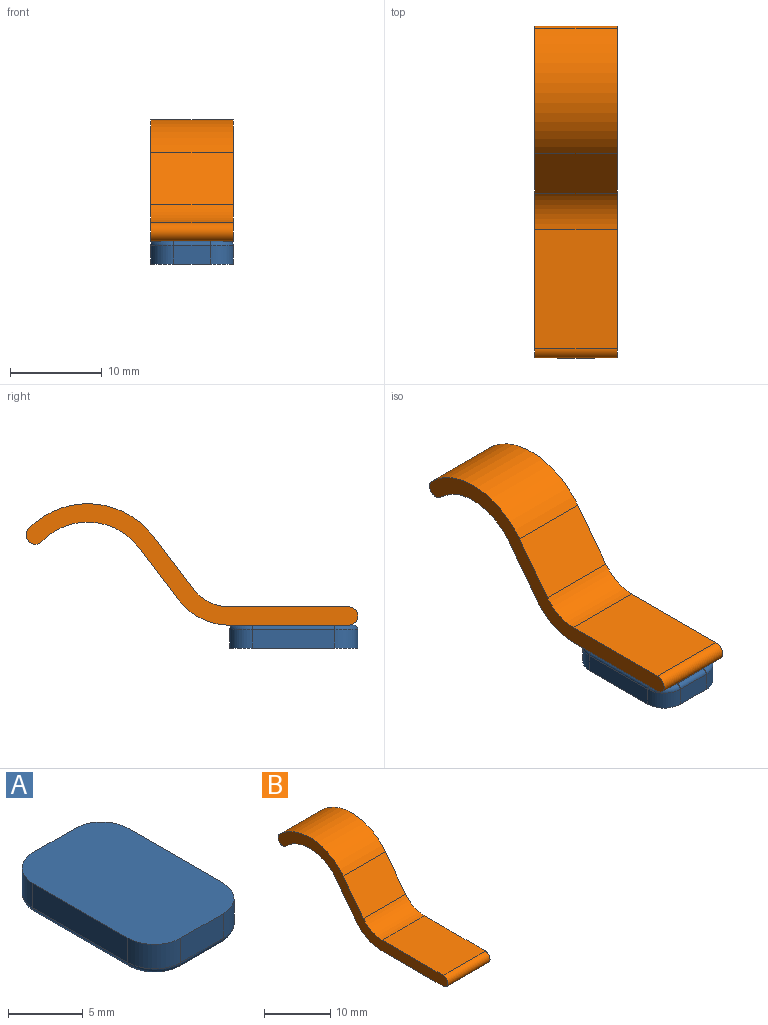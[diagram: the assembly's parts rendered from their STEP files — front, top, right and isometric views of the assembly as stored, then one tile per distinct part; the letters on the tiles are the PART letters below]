
ASSEMBLY  parts=2 mates=1
PART A: 27 faces, bbox 9.4x14.4x2.5 mm
  f0: plane 9x2mm, normal (1,0,0), area 18mm2, adj f1,f7,f8,f17
  f1: cylinder r=2.5mm len=2.5mm, axis (0,0,-1), area 7.9mm2, adj f0,f2,f8,f15
  f2: plane 4x2mm, normal (0,1,0), area 8mm2, adj f1,f3,f8,f16
  f3: cylinder r=2.5mm len=2.5mm, axis (0,0,-1), area 7.9mm2, adj f2,f4,f8,f18
  f4: plane 9x2mm, normal (-1,0,0), area 18mm2, adj f3,f5,f8,f20
  f5: cylinder r=2.5mm len=2.5mm, axis (0,0,-1), area 7.9mm2, adj f4,f6,f8,f22
  f6: plane 4x2mm, normal (0,-1,0), area 8mm2, adj f5,f7,f8,f21
  f7: cylinder r=2.5mm len=2.5mm, axis (0,0,-1), area 7.9mm2, adj f0,f6,f8,f19
  f8: plane 14x9mm, normal (0,0,1), area 120.6mm2, adj f0,f1,f2,f3,f4,f5,f6,f7
  f9: plane 13x8mm, normal (0,0,-1), area 53.4mm2, adj f15,f16,f17,f18,f19,f20,f21,f22
  f10: cylinder r=2.5mm len=5mm, axis (0,0,-1), area 11.8mm2, adj f11,f13,f14,f26
  f11: cylinder r=1.04mm len=1.46mm, axis (0,0,-1), area 1.6mm2, adj f10,f12,f14,f24
  f12: cylinder r=2.5mm len=5mm, axis (0,0,-1), area 11.8mm2, adj f11,f13,f14,f23
  f13: cylinder r=1.04mm len=1.46mm, axis (0,0,-1), area 1.6mm2, adj f10,f12,f14,f25
  f14: plane 10x5mm, normal (0,0,-1), area 40.3mm2, adj f10,f11,f12,f13
  f15: torus R=2mm, axis (0,0,1), area 2.9mm2, adj f1,f9,f16,f17
  f16: cylinder r=0.5mm len=4mm, axis (-1,0,0), area 3.1mm2, adj f2,f9,f15,f18
  f17: cylinder r=0.5mm len=9mm, axis (0,1,0), area 7.1mm2, adj f0,f9,f15,f19
  f18: torus R=2mm, axis (0,0,1), area 2.9mm2, adj f3,f9,f16,f20
  f19: torus R=2mm, axis (0,0,1), area 2.9mm2, adj f7,f9,f17,f21
  f20: cylinder r=0.5mm len=9mm, axis (0,-1,0), area 7.1mm2, adj f4,f9,f18,f22
  f21: cylinder r=0.5mm len=4mm, axis (1,0,0), area 3.1mm2, adj f6,f9,f19,f22
  f22: torus R=2mm, axis (0,0,1), area 2.9mm2, adj f5,f9,f20,f21
  f23: torus R=2.75mm, axis (0,0,1), area 4.8mm2, adj f9,f12,f24,f25
  f24: torus R=0.79mm, axis (0,0,1), area 0.6mm2, adj f9,f11,f23,f26
  f25: torus R=0.79mm, axis (0,0,1), area 0.6mm2, adj f9,f13,f23,f26
  f26: torus R=2.75mm, axis (0,0,1), area 4.8mm2, adj f9,f10,f24,f25
PART B: 23 faces, bbox 9x36.2x13.3 mm
  f0: plane 9x5.7mm, normal (0,-0.8,0.6), area 64.4mm2, adj f1,f7,f8,f9
  f1: cylinder r=5mm len=9mm, axis (-1,0,0), area 41.5mm2, adj f0,f2,f8,f9
  f2: plane 13x9mm, normal (0,0,1), area 117mm2, adj f1,f8,f9,f21
  f3: plane 13x9mm, normal (0,0,-1), area 69.8mm2, adj f4,f8,f9,f15,f16,f17,f18,f21
  f4: cylinder r=7mm len=9mm, axis (-1,0,0), area 58.1mm2, adj f3,f5,f8,f9
  f5: plane 9x5.7mm, normal (0,0.8,-0.6), area 64.4mm2, adj f4,f6,f8,f9
  f6: cylinder r=7mm len=10.59mm, axis (-1,0,0), area 108.4mm2, adj f5,f8,f9,f22
  f7: cylinder r=9mm len=13.61mm, axis (-1,0,0), area 139.3mm2, adj f0,f8,f9,f22
  f8: plane 36.2x13.25mm, normal (1,0,0), area 82mm2, adj f0,f1,f2,f3,f4,f5,f6,f7
  f9: plane 36.2x13.25mm, normal (-1,0,0), area 82mm2, adj f0,f1,f2,f3,f4,f5,f6,f7
  f10: cylinder r=2.5mm len=5mm, axis (0,0,-1), area 11.4mm2, adj f11,f13,f14,f15,f19,f20
  f11: cylinder r=1.04mm len=1.46mm, axis (0,0,-1), area 0.8mm2, adj f10,f12,f16,f19
  f12: cylinder r=2.5mm len=5mm, axis (0,0,-1), area 11.4mm2, adj f11,f13,f14,f18,f19,f20
  f13: cylinder r=1.04mm len=1.46mm, axis (0,0,-1), area 0.8mm2, adj f10,f12,f17,f20
  f14: plane 10x5mm, normal (0,0,-1), area 37mm2, adj f10,f12,f19,f20
  f15: torus R=2.75mm, axis (0,0,1), area 4.8mm2, adj f3,f10,f16,f17
  f16: torus R=0.79mm, axis (0,0,1), area 0.6mm2, adj f3,f11,f15,f18
  f17: torus R=0.79mm, axis (0,0,1), area 0.6mm2, adj f3,f13,f15,f18
  f18: torus R=2.75mm, axis (0,0,1), area 4.8mm2, adj f3,f12,f16,f17
  f19: torus R=1.54mm, axis (0,0,1), area 2.3mm2, adj f10,f11,f12,f14
  f20: torus R=1.54mm, axis (0,0,1), area 2.3mm2, adj f10,f12,f13,f14
  f21: cylinder r=1mm len=9mm, axis (1,0,0), area 28.3mm2, adj f2,f3,f8,f9
  f22: cylinder r=1mm len=9mm, axis (-1,0,0), area 28.3mm2, adj f6,f7,f8,f9
PLACE A rot(axis=(0,1,0),180deg) t=(-2.5,-7.5,2.5)mm
PLACE B t=(-7,-14.5,2.5)mm
MATE fastened A.f12 <-> B.f12  axis (0,0,1) through (-2.5,-10,2.5)mm
